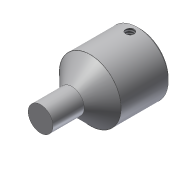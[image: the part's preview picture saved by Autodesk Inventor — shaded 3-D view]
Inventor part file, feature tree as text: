
AUTODESK INVENTOR PART (.ipt)
format: ipt  version: unknown  size: 202,240 bytes
history: native  units: in
note: dims shown in document units (in); Inventor stores cm internally (conversion verified against a paired STEP export)
features: sketch x5, extrude x3, chamfer x2, plane x1, hole x1
ambient origin geometry x8: Origin, YZ Plane, XZ Plane, XY Plane, X Axis, Y Axis, Z Axis, Center Point
feature tree (12):
  extrude  "Extrusion1"  Depth=1.0in TaperAngle=0.0deg
  extrude  "Extrusion2"  Depth=0.5in TaperAngle=0.0deg
  extrude  "Extrusion3"  Depth=0.3in TaperAngle=0.0deg
  sketch  "Sketch4"  dims[d9=0.1in]
  plane  "Work Plane1"
  hole  "Hole1"  [1 undecoded]
  chamfer  "Chamfer1"  Distance=0.025in Angle=45.0deg
  chamfer  "Chamfer2"  [1 undecoded]
  sketch  "Sketch1"  dims[d0=0.625in d1=1.0in d2=0.0in]
  sketch  "Sketch2"  dims[d3=0.25in d4=0.5in d5=0.0in]
  sketch  "Sketch3"  dims[d6=0.338in d7=0.3in d8=0.0in]
  sketch  "Sketch5"  dims[d10=0.085in d11=0.5in d12=0.375in d13=0.25in d14=0.5635in d15=0.75in d16=0.8108in d17=0.185in d18=0.125in d19=45.0deg d20=0.025in d21=0.125in d22=45.0deg]
note: 2 required parameter values undecoded (feature->parameter linkage not recoverable at this tier; creation-order binding heuristic only, values carry confidence <= 0.55)
